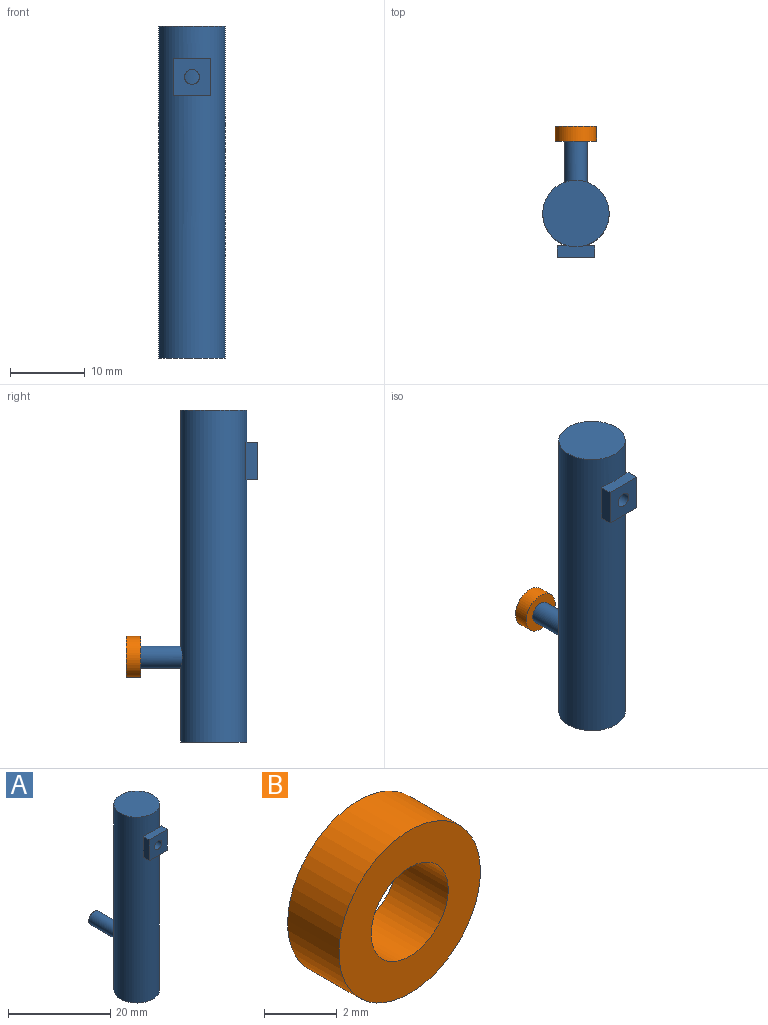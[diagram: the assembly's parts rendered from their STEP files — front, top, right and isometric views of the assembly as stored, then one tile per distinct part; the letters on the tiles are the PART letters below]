
ASSEMBLY  parts=2 mates=1
PART A: 14 faces, bbox 8.9x17.7x44.5 mm
  f0: cylinder r=4.45mm len=44.45mm, axis (0,0,-1), area 1223.6mm2, adj f1,f2,f4,f5,f7,f9,f12
  f1: plane 8.89x8.89mm, normal (0,0,1), area 62.1mm2, adj f0
  f2: plane 8.89x8.89mm, normal (0,0,-1), area 62.1mm2, adj f0
  f3: cylinder r=1mm len=2mm, axis (0,-1,0), area 9.6mm2, adj f10,f11
  f4: plane 5x1.45mm, normal (0,1,0), area 7.2mm2, adj f0,f7,f8,f9
  f5: plane 5x1.45mm, normal (0,1,0), area 7.2mm2, adj f0,f6,f7,f9
  f6: plane 5x1.6mm, normal (1,0,0), area 8mm2, adj f5,f7,f9,f10
  f7: plane 5x1.6mm, normal (0,0,1), area 7.8mm2, adj f0,f4,f5,f6,f8,f10
  f8: plane 5x1.6mm, normal (-1,0,0), area 8mm2, adj f4,f7,f9,f10
  f9: plane 5x1.6mm, normal (0,0,-1), area 7.8mm2, adj f0,f4,f5,f6,f8,f10
  f10: plane 5x5mm, normal (0,-1,0), area 21.9mm2, adj f3,f6,f7,f8,f9
  f11: cylinder r=4.45mm len=2mm, axis (0,0,-1), area 3.2mm2, adj f3
  f12: cylinder r=1.5mm len=7.56mm, axis (0,-1,0), area 70mm2, adj f0,f13
  f13: plane 3x3mm, normal (0,1,0), area 7.1mm2, adj f12
PART B: 4 faces, bbox 5.5x2x5.5 mm
  f0: cylinder r=1.5mm len=3mm, axis (0,1,0), area 18.8mm2, adj f2,f3
  f1: cylinder r=2.75mm len=5.5mm, axis (0,1,0), area 34.6mm2, adj f2,f3
  f2: plane 5.5x5.5mm, normal (0,-1,0), area 16.7mm2, adj f0,f1
  f3: plane 5.5x5.5mm, normal (0,1,0), area 16.7mm2, adj f0,f1
PLACE A t=(8.78,0,2.64)mm
PLACE B rot(axis=(0,-1,0),131.9deg) t=(8.78,25.4,7.69)mm
MATE revolute B.f0 <-> A.f12  axis (0,1,0) through (8.78,25.4,7.69)mm
